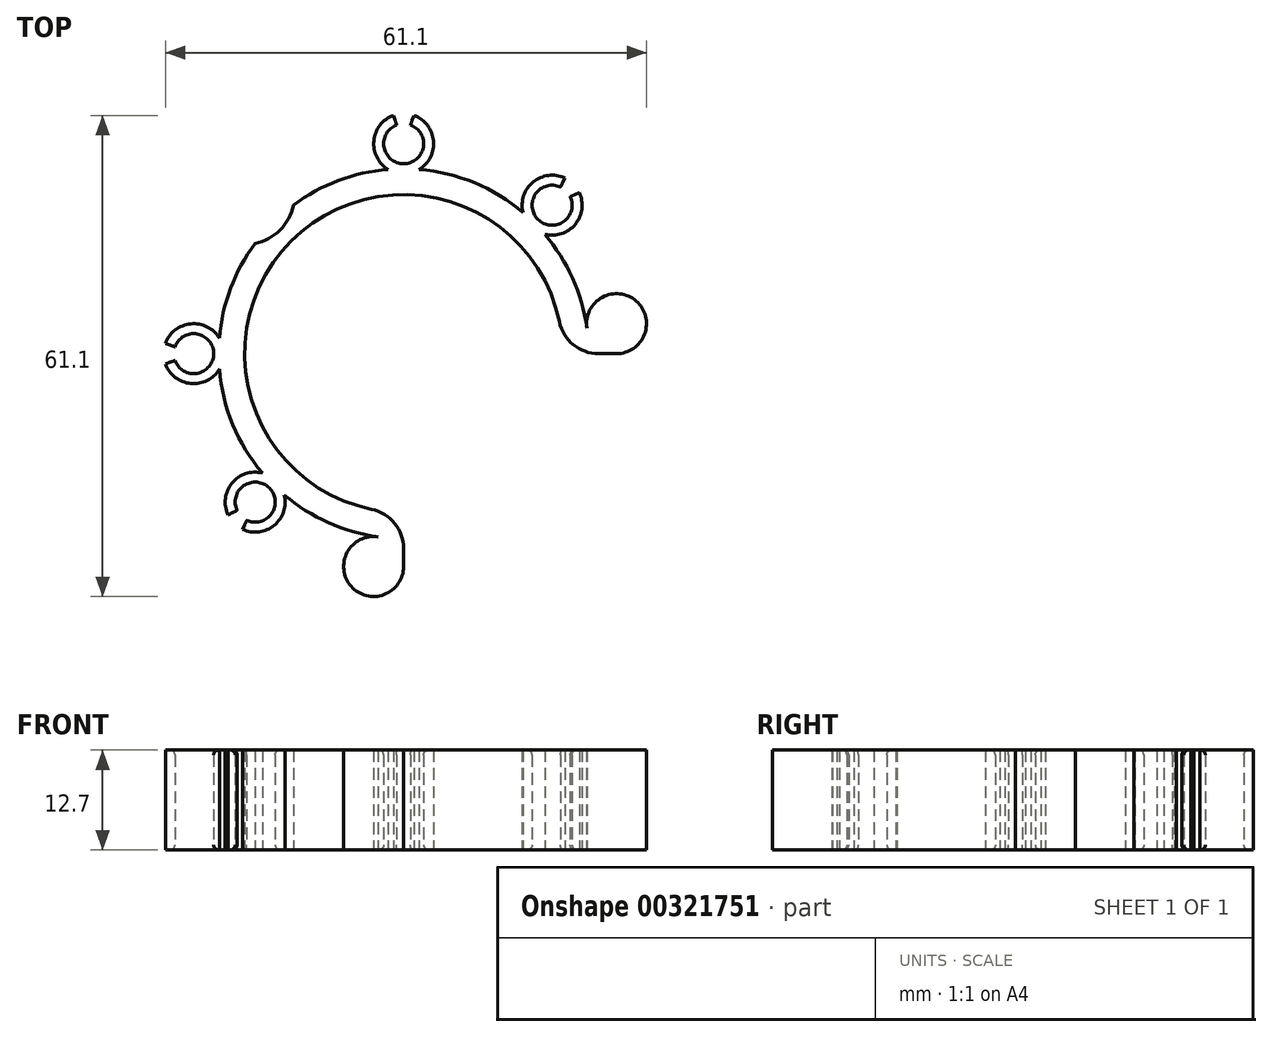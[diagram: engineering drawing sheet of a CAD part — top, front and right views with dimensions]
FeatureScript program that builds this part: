
annotation { "Feature Type Name" : "Feature", "Feature Type Description" : "" }
export const myFeature = defineFeature(function(context is Context, id is Id, definition is map)
    precondition{}
    {
        {
            var Q0;
            Q0=qCreatedBy(makeId("Top.planeOp"),FACE);
            var sketch = newSketch(context, id + "F0", { "sketchPlane" : qUnion([Q0])});
            skCircle(sketch, "E0", {"center": v(0, 0) * mm, "radius": 20.2 * mm});
            skCircle(sketch, "E1", {"center": v(0, 0) * mm, "radius": 23.5 * mm});
            skLineSegment(sketch, "E2", {"start": v(23.5, 0) * mm, "end": v(20.2, 0) * mm});
            skLineSegment(sketch, "E3", {"start": v(0, -23.5) * mm, "end": v(0, -20.2) * mm});
            skCircle(sketch, "E4", {"center": v(27.04, 3.81) * mm, "radius": 3.81 * mm});
            skLineSegment(sketch, "E5", {"start": v(23.5, 0) * mm, "end": v(27.04, 0) * mm});
            skCircle(sketch, "E6", {"center": v(-3.8, -27.04) * mm, "radius": 3.81 * mm});
            skLineSegment(sketch, "E7", {"start": v(0, -23.5) * mm, "end": v(0, -27.04) * mm});
            skArc(sketch, "E8", {"start": v(20.2, 0) * mm, "mid": v(14.28, -14.28) * mm, "end": v(0, -20.2) * mm});
            skPoint(sketch, "E9", {"position": v(14.28, -14.28) * mm});
            skLineSegment(sketch, "E10", {"start": v(14.28, -14.28) * mm, "end": v(0, 0) * mm});
            skLineSegment(sketch, "E11", {"start": v(0, 0) * mm, "end": v(-16.61, 16.61) * mm});
            skLineSegment(sketch, "E12", {"start": v(-16.61, 16.61) * mm, "end": v(-20.2, 20.2) * mm});
            skCircle(sketch, "E13", {"center": v(-20.2, 20.2) * mm, "radius": 6.35 * mm});
            skLineSegment(sketch, "E14", {"start": v(0, 0) * mm, "end": v(-18.86, -18.86) * mm});
            skCircle(sketch, "E15", {"center": v(-18.86, -18.86) * mm, "radius": 3.81 * mm});
            skCircle(sketch, "E16", {"center": v(-18.86, -18.86) * mm, "radius": 2.54 * mm});
            skLineSegment(sketch, "E17", {"start": v(-18.86, -18.86) * mm, "end": v(-21.55, -21.55) * mm});
            skLineSegment(sketch, "E18", {"start": v(-18.86, -18.86) * mm, "end": v(-22.31, -20.47) * mm});
            skLineSegment(sketch, "E19", {"start": v(-18.86, -18.86) * mm, "end": v(-20.47, -22.31) * mm});
            skCircle(sketch, "E20.1.0", {"center": v(-26.67, 0) * mm, "radius": 3.81 * mm});
            skLineSegment(sketch, "E20.1.1", {"start": v(-26.67, 0) * mm, "end": v(-30.25, -1.3) * mm});
            skCircle(sketch, "E20.1.2", {"center": v(-26.67, 0) * mm, "radius": 2.54 * mm});
            skLineSegment(sketch, "E20.1.3", {"start": v(-26.67, 0) * mm, "end": v(-30.25, 1.3) * mm});
            skLineSegment(sketch, "E20.anchor1", {"start": v(0, 0) * mm, "end": v(-22.31, -20.47) * mm, "construction": true});
            skLineSegment(sketch, "E20.anchor2", {"start": v(0, 0) * mm, "end": v(-30.25, 1.3) * mm, "construction": true});
            skLineSegment(sketch, "E21.1.0", {"start": v(0, 26.67) * mm, "end": v(-1.3, 30.25) * mm});
            skCircle(sketch, "E21.1.1", {"center": v(0, 26.67) * mm, "radius": 3.81 * mm});
            skLineSegment(sketch, "E21.1.2", {"start": v(0, 26.67) * mm, "end": v(1.3, 30.25) * mm});
            skCircle(sketch, "E21.1.3", {"center": v(0, 26.67) * mm, "radius": 2.54 * mm});
            skLineSegment(sketch, "E21.anchor1", {"start": v(0, 0) * mm, "end": v(-30.25, -1.3) * mm, "construction": true});
            skLineSegment(sketch, "E21.anchor2", {"start": v(0, 0) * mm, "end": v(-1.3, 30.25) * mm, "construction": true});
            skLineSegment(sketch, "E22.1.0", {"start": v(18.86, 18.86) * mm, "end": v(20.47, 22.31) * mm});
            skCircle(sketch, "E22.1.1", {"center": v(18.86, 18.86) * mm, "radius": 2.54 * mm});
            skLineSegment(sketch, "E22.1.2", {"start": v(18.86, 18.86) * mm, "end": v(22.31, 20.47) * mm});
            skCircle(sketch, "E22.1.3", {"center": v(18.86, 18.86) * mm, "radius": 3.81 * mm});
            skLineSegment(sketch, "E22.anchor2", {"start": v(0, 0) * mm, "end": v(20.47, 22.31) * mm, "construction": true});
            skSolve(sketch);
        }
        {
            var Q0;
            {var subQ0=sQuery(id+"F0.wireOp",EDGE,"E6");var subQ1=makeQuery(id+"F0.imprint","INTERSECT",VERTEX,{"derivedFrom":[subQ0,sQuery(id+"F0.wireOp",EDGE,"E7")]});Q0=makeQuery(id+"F0.imprint","IMPRINT",FACE,{"disambiguationData":[TD([[makeQuery(id+"F0.imprint","IMPRINT",EDGE,{"disambiguationData":[TD([[subQ1,-1.0]])],"derivedFrom":subQ0}),1.0]])]});}
            var Q1;
            {var subQ0=sQuery(id+"F0.wireOp",EDGE,"E7");Q1=makeQuery(id+"F0.imprint","IMPRINT",FACE,{"disambiguationData":[TD([[makeQuery(id+"F0.imprint","IMPRINT",EDGE,{"derivedFrom":subQ0}),-1.0]])]});}
            var Q2;
            {var subQ0=sQuery(id+"F0.wireOp",EDGE,"E4");var subQ1=makeQuery(id+"F0.imprint","INTERSECT",VERTEX,{"derivedFrom":[subQ0,sQuery(id+"F0.wireOp",EDGE,"E5")]});Q2=makeQuery(id+"F0.imprint","IMPRINT",FACE,{"disambiguationData":[TD([[makeQuery(id+"F0.imprint","IMPRINT",EDGE,{"disambiguationData":[TD([[subQ1,1.0]])],"derivedFrom":subQ0}),1.0]])]});}
            var Q3;
            {var subQ4=sQuery(id+"F0.wireOp",EDGE,"E2");Q3=makeQuery(id+"F0.imprint","IMPRINT",FACE,{"disambiguationData":[TD([[makeQuery(id+"F0.imprint","IMPRINT",EDGE,{"derivedFrom":subQ4}),-1.0]])]});}
            var Q4;
            {var subQ0=sQuery(id+"F0.wireOp",EDGE,"E5");Q4=makeQuery(id+"F0.imprint","IMPRINT",FACE,{"disambiguationData":[TD([[makeQuery(id+"F0.imprint","IMPRINT",EDGE,{"derivedFrom":subQ0}),1.0]])]});}
            var Q5;
            {var subQ0=sQuery(id+"F0.wireOp",EDGE,"E3");Q5=makeQuery(id+"F0.imprint","IMPRINT",FACE,{"disambiguationData":[TD([[makeQuery(id+"F0.imprint","IMPRINT",EDGE,{"derivedFrom":subQ0}),1.0]])]});}
            var Q6;
            {var subQ3=sQuery(id+"F0.wireOp",EDGE,"E11");var subQ5=sQuery(id+"F0.wireOp",EDGE,"E0");var subQ6=makeQuery(id+"F0.imprint","INTERSECT",VERTEX,{"derivedFrom":[subQ5,subQ3]});Q6=makeQuery(id+"F0.imprint","IMPRINT",FACE,{"disambiguationData":[TD([[makeQuery(id+"F0.imprint","IMPRINT",EDGE,{"disambiguationData":[TD([[subQ6,-1.0]])],"derivedFrom":subQ5}),-1.0]])]});}
            var Q7;
            {var subQ1=sQuery(id+"F0.wireOp",EDGE,"E14");var subQ3=sQuery(id+"F0.wireOp",EDGE,"E16");var subQ4=makeQuery(id+"F0.imprint","INTERSECT",VERTEX,{"derivedFrom":[subQ1,subQ3]});Q7=makeQuery(id+"F0.imprint","IMPRINT",FACE,{"disambiguationData":[TD([[makeQuery(id+"F0.imprint","IMPRINT",EDGE,{"disambiguationData":[TD([[subQ4,1.0]])],"derivedFrom":subQ3}),-1.0]])]});}
            var Q8;
            {var subQ1=sQuery(id+"F0.wireOp",EDGE,"E14");var subQ3=sQuery(id+"F0.wireOp",EDGE,"E16");var subQ4=makeQuery(id+"F0.imprint","INTERSECT",VERTEX,{"derivedFrom":[subQ1,subQ3]});Q8=makeQuery(id+"F0.imprint","IMPRINT",FACE,{"disambiguationData":[TD([[makeQuery(id+"F0.imprint","IMPRINT",EDGE,{"disambiguationData":[TD([[subQ4,-1.0]])],"derivedFrom":subQ3}),-1.0]])]});}
            var Q9;
            {var subQ0=sQuery(id+"F0.wireOp",EDGE,"E15");var subQ1=sQuery(id+"F0.wireOp",EDGE,"E1");var subQ2=makeQuery(id+"F0.imprint","INTERSECT",VERTEX,{"disambiguationData":[OD(1.0)],"derivedFrom":[subQ1,subQ0]});Q9=makeQuery(id+"F0.imprint","IMPRINT",FACE,{"disambiguationData":[TD([[makeQuery(id+"F0.imprint","IMPRINT",EDGE,{"disambiguationData":[TD([[subQ2,1.0]])],"derivedFrom":subQ1}),1.0]])]});}
            var Q10;
            {var subQ0=sQuery(id+"F0.wireOp",EDGE,"E15");var subQ1=sQuery(id+"F0.wireOp",EDGE,"E1");var subQ2=makeQuery(id+"F0.imprint","INTERSECT",VERTEX,{"disambiguationData":[OD(0.0)],"derivedFrom":[subQ1,subQ0]});Q10=makeQuery(id+"F0.imprint","IMPRINT",FACE,{"disambiguationData":[TD([[makeQuery(id+"F0.imprint","IMPRINT",EDGE,{"disambiguationData":[TD([[subQ2,-1.0]])],"derivedFrom":subQ1}),1.0]])]});}
            var Q11;
            {var subQ0=sQuery(id+"F0.wireOp",EDGE,"E20.1.0");var subQ1=sQuery(id+"F0.wireOp",EDGE,"E1");var subQ2=makeQuery(id+"F0.imprint","INTERSECT",VERTEX,{"disambiguationData":[OD(0.0)],"derivedFrom":[subQ1,subQ0]});Q11=makeQuery(id+"F0.imprint","IMPRINT",FACE,{"disambiguationData":[TD([[makeQuery(id+"F0.imprint","IMPRINT",EDGE,{"disambiguationData":[TD([[subQ2,-1.0]])],"derivedFrom":subQ1}),1.0]])]});}
            var Q12;
            {var subQ1=sQuery(id+"F0.wireOp",EDGE,"E20.1.0");var subQ5=sQuery(id+"F0.wireOp",EDGE,"E1");var subQ9=makeQuery(id+"F0.imprint","INTERSECT",VERTEX,{"disambiguationData":[OD(0.0)],"derivedFrom":[subQ5,subQ1]});Q12=makeQuery(id+"F0.imprint","IMPRINT",FACE,{"disambiguationData":[TD([[makeQuery(id+"F0.imprint","IMPRINT",EDGE,{"disambiguationData":[TD([[subQ9,-1.0]])],"derivedFrom":subQ5}),-1.0]])]});}
            var Q13;
            {var subQ0=sQuery(id+"F0.wireOp",EDGE,"E21.1.1");var subQ1=sQuery(id+"F0.wireOp",EDGE,"E1");var subQ2=makeQuery(id+"F0.imprint","INTERSECT",VERTEX,{"disambiguationData":[OD(0.0)],"derivedFrom":[subQ1,subQ0]});Q13=makeQuery(id+"F0.imprint","IMPRINT",FACE,{"disambiguationData":[TD([[makeQuery(id+"F0.imprint","IMPRINT",EDGE,{"disambiguationData":[TD([[subQ2,-1.0]])],"derivedFrom":subQ1}),1.0]])]});}
            var Q14;
            {var subQ0=sQuery(id+"F0.wireOp",EDGE,"E21.1.1");var subQ3=sQuery(id+"F0.wireOp",EDGE,"E1");var subQ7=makeQuery(id+"F0.imprint","INTERSECT",VERTEX,{"disambiguationData":[OD(0.0)],"derivedFrom":[subQ3,subQ0]});Q14=makeQuery(id+"F0.imprint","IMPRINT",FACE,{"disambiguationData":[TD([[makeQuery(id+"F0.imprint","IMPRINT",EDGE,{"disambiguationData":[TD([[subQ7,-1.0]])],"derivedFrom":subQ3}),-1.0]])]});}
            var Q15;
            {var subQ0=sQuery(id+"F0.wireOp",EDGE,"E22.1.3");var subQ1=sQuery(id+"F0.wireOp",EDGE,"E1");var subQ2=makeQuery(id+"F0.imprint","INTERSECT",VERTEX,{"disambiguationData":[OD(0.0)],"derivedFrom":[subQ1,subQ0]});Q15=makeQuery(id+"F0.imprint","IMPRINT",FACE,{"disambiguationData":[TD([[makeQuery(id+"F0.imprint","IMPRINT",EDGE,{"disambiguationData":[TD([[subQ2,-1.0]])],"derivedFrom":subQ1}),1.0]])]});}
            var Q16;
            {var subQ5=sQuery(id+"F0.wireOp",EDGE,"E22.1.3");var subQ8=sQuery(id+"F0.wireOp",EDGE,"E1");var subQ9=makeQuery(id+"F0.imprint","INTERSECT",VERTEX,{"disambiguationData":[OD(0.0)],"derivedFrom":[subQ8,subQ5]});Q16=makeQuery(id+"F0.imprint","IMPRINT",FACE,{"disambiguationData":[TD([[makeQuery(id+"F0.imprint","IMPRINT",EDGE,{"disambiguationData":[TD([[subQ9,-1.0]])],"derivedFrom":subQ8}),-1.0]])]});}
            extrude(context, id + "F1", {"entities" : qUnion([Q0, Q1, Q2, Q3, Q4, Q5, Q6, Q7, Q8, Q9, Q10, Q11, Q12, Q13, Q14, Q15, Q16]), "depth" : 12.7 * mm});
        }
        {
            var Q0;
            Q0=makeQuery(id+"F1.opExtrude","SWEPT_EDGE",EDGE,{"disambiguationData":[OSD([sQuery(id+"F0.wireOp",EDGE,"E0"),sQuery(id+"F0.wireOp",EDGE,"E3")])]});
            var Q1;
            Q1=makeQuery(id+"F1.opExtrude","SWEPT_EDGE",EDGE,{"disambiguationData":[OSD([sQuery(id+"F0.wireOp",EDGE,"E0"),sQuery(id+"F0.wireOp",EDGE,"E2")])]});
            fillet(context, id + "F2", {"entities" : qUnion([Q0, Q1]), "radius" : 5.08 * mm, "tangentPropagation" : true, "allowEdgeOverflow" : false});
        }
        {
            var Q0;
            Q0=makeQuery(id+"F1.opExtrude","CAP_EDGE",EDGE,{"disambiguationData":[OSD([sQuery(id+"F0.wireOp",EDGE,"E20.1.2")])],"isStart":false});
            var Q1;
            Q1=makeQuery(id+"F1.opExtrude","CAP_EDGE",EDGE,{"disambiguationData":[OSD([sQuery(id+"F0.wireOp",EDGE,"E16")])],"isStart":false});
            var Q2;
            Q2=makeQuery(id+"F1.opExtrude","CAP_EDGE",EDGE,{"disambiguationData":[OSD([sQuery(id+"F0.wireOp",EDGE,"E21.1.3")])],"isStart":false});
            var Q3;
            Q3=makeQuery(id+"F1.opExtrude","CAP_EDGE",EDGE,{"disambiguationData":[OSD([sQuery(id+"F0.wireOp",EDGE,"E22.1.1")])],"isStart":false});
            var Q4;
            Q4=makeQuery(id+"F1.opExtrude","CAP_EDGE",EDGE,{"disambiguationData":[OSD([sQuery(id+"F0.wireOp",EDGE,"E16")])],"isStart":true});
            var Q5;
            Q5=makeQuery(id+"F1.opExtrude","CAP_EDGE",EDGE,{"disambiguationData":[OSD([sQuery(id+"F0.wireOp",EDGE,"E20.1.2")])],"isStart":true});
            var Q6;
            Q6=makeQuery(id+"F1.opExtrude","CAP_EDGE",EDGE,{"disambiguationData":[OSD([sQuery(id+"F0.wireOp",EDGE,"E22.1.1")])],"isStart":true});
            var Q7;
            Q7=makeQuery(id+"F1.opExtrude","CAP_EDGE",EDGE,{"disambiguationData":[OSD([sQuery(id+"F0.wireOp",EDGE,"E21.1.3")])],"isStart":true});
            fillet(context, id + "F3", {"entities" : qUnion([Q0, Q1, Q2, Q3, Q4, Q5, Q6, Q7]), "radius" : 0.64 * mm, "tangentPropagation" : true, "allowEdgeOverflow" : false});
        }
    });
